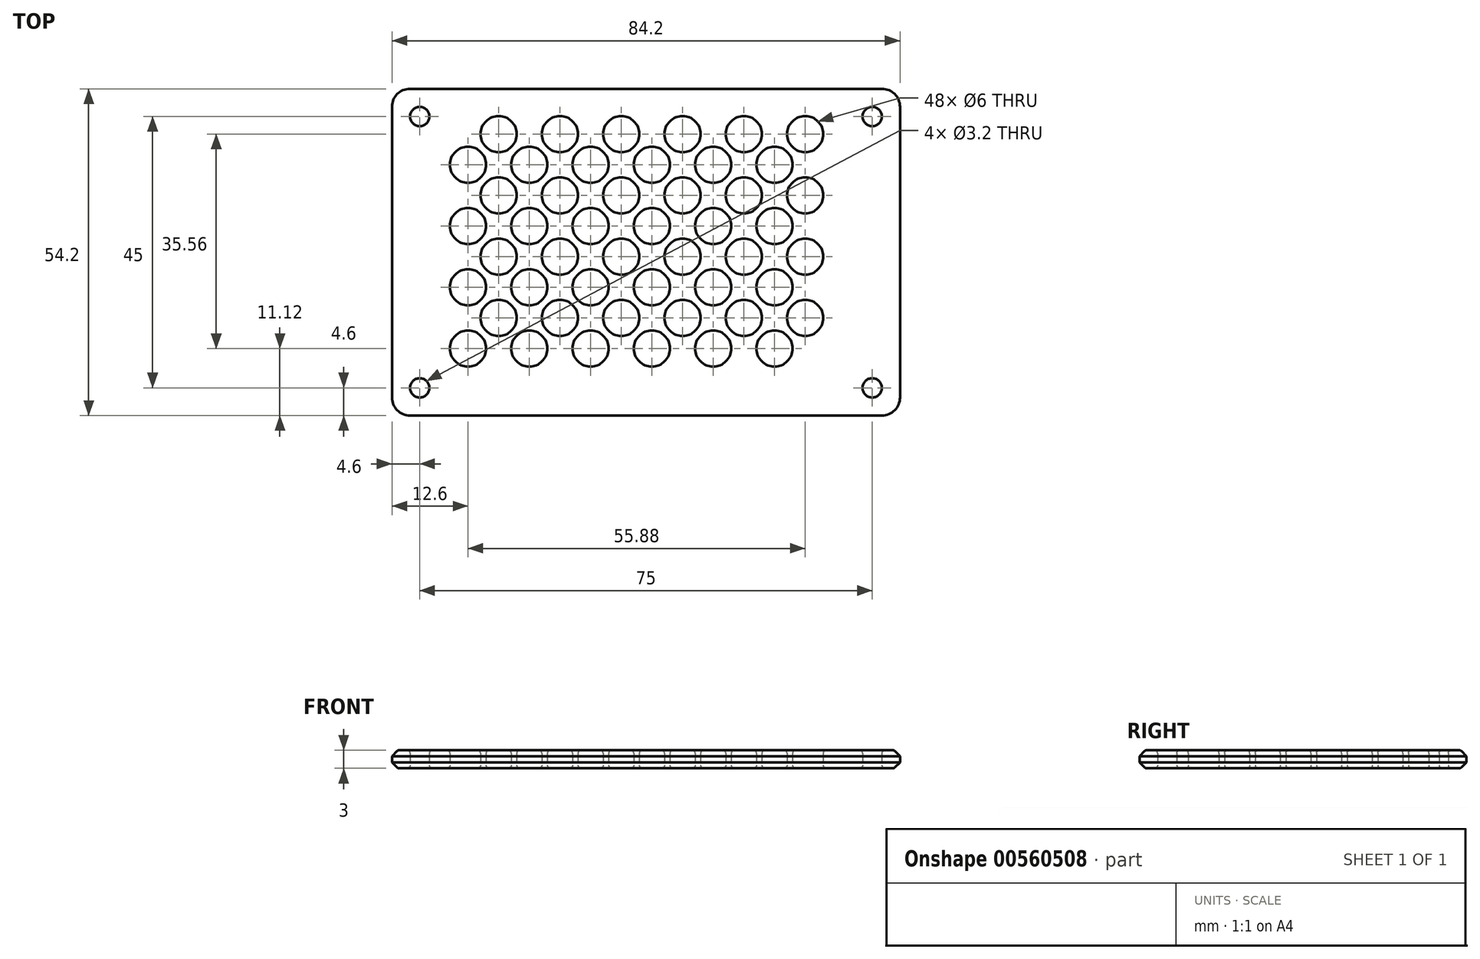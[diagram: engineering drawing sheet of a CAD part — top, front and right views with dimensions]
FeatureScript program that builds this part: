
annotation { "Feature Type Name" : "Feature", "Feature Type Description" : "" }
export const myFeature = defineFeature(function(context is Context, id is Id, definition is map)
    precondition{}
    {
        {
            var Q0;
            Q0=qCreatedBy(makeId("Top.planeOp"),FACE);
            var sketch = newSketch(context, id + "F0", { "sketchPlane" : qUnion([Q0])});
            skLineSegment(sketch, "E0.bottom", {"start": v(-42.1, 27.1) * mm, "end": v(42.1, 27.1) * mm});
            skLineSegment(sketch, "E0.top", {"start": v(-42.1, -27.1) * mm, "end": v(42.1, -27.1) * mm});
            skLineSegment(sketch, "E0.left", {"start": v(-42.1, 27.1) * mm, "end": v(-42.1, -27.1) * mm});
            skLineSegment(sketch, "E0.right", {"start": v(42.1, 27.1) * mm, "end": v(42.1, -27.1) * mm});
            skPoint(sketch, "E0.middle", {"position": v(0, 0) * mm});
            skCircle(sketch, "E1", {"center": v(-37.5, 22.5) * mm, "radius": 1.6 * mm});
            skCircle(sketch, "E2", {"center": v(-29.5, 14.5) * mm, "radius": 3 * mm});
            skCircle(sketch, "E3", {"center": v(-24.42, 19.58) * mm, "radius": 3 * mm});
            skCircle(sketch, "E4.0.1.0", {"center": v(-24.42, 9.42) * mm, "radius": 3 * mm});
            skCircle(sketch, "E4.0.1.1", {"center": v(-29.5, 4.34) * mm, "radius": 3 * mm});
            skCircle(sketch, "E4.0.2.0", {"center": v(-24.42, -0.74) * mm, "radius": 3 * mm});
            skCircle(sketch, "E4.0.2.1", {"center": v(-29.5, -5.82) * mm, "radius": 3 * mm});
            skCircle(sketch, "E4.0.3.0", {"center": v(-24.42, -10.9) * mm, "radius": 3 * mm});
            skCircle(sketch, "E4.0.3.1", {"center": v(-29.5, -15.98) * mm, "radius": 3 * mm});
            skCircle(sketch, "E4.1.0.0", {"center": v(-14.26, 19.58) * mm, "radius": 3 * mm});
            skCircle(sketch, "E4.1.0.1", {"center": v(-19.34, 14.5) * mm, "radius": 3 * mm});
            skCircle(sketch, "E4.1.1.0", {"center": v(-14.26, 9.42) * mm, "radius": 3 * mm});
            skCircle(sketch, "E4.1.1.1", {"center": v(-19.34, 4.34) * mm, "radius": 3 * mm});
            skCircle(sketch, "E4.1.2.0", {"center": v(-14.26, -0.74) * mm, "radius": 3 * mm});
            skCircle(sketch, "E4.1.2.1", {"center": v(-19.34, -5.82) * mm, "radius": 3 * mm});
            skCircle(sketch, "E4.1.3.0", {"center": v(-14.26, -10.9) * mm, "radius": 3 * mm});
            skCircle(sketch, "E4.1.3.1", {"center": v(-19.34, -15.98) * mm, "radius": 3 * mm});
            skCircle(sketch, "E4.2.0.0", {"center": v(-4.1, 19.58) * mm, "radius": 3 * mm});
            skCircle(sketch, "E4.2.0.1", {"center": v(-9.18, 14.5) * mm, "radius": 3 * mm});
            skCircle(sketch, "E4.2.1.0", {"center": v(-4.1, 9.42) * mm, "radius": 3 * mm});
            skCircle(sketch, "E4.2.1.1", {"center": v(-9.18, 4.34) * mm, "radius": 3 * mm});
            skCircle(sketch, "E4.2.2.0", {"center": v(-4.1, -0.74) * mm, "radius": 3 * mm});
            skCircle(sketch, "E4.2.2.1", {"center": v(-9.18, -5.82) * mm, "radius": 3 * mm});
            skCircle(sketch, "E4.2.3.0", {"center": v(-4.1, -10.9) * mm, "radius": 3 * mm});
            skCircle(sketch, "E4.2.3.1", {"center": v(-9.18, -15.98) * mm, "radius": 3 * mm});
            skCircle(sketch, "E4.3.0.0", {"center": v(6.06, 19.58) * mm, "radius": 3 * mm});
            skCircle(sketch, "E4.3.0.1", {"center": v(0.98, 14.5) * mm, "radius": 3 * mm});
            skCircle(sketch, "E4.3.1.0", {"center": v(6.06, 9.42) * mm, "radius": 3 * mm});
            skCircle(sketch, "E4.3.1.1", {"center": v(0.98, 4.34) * mm, "radius": 3 * mm});
            skCircle(sketch, "E4.3.2.0", {"center": v(6.06, -0.74) * mm, "radius": 3 * mm});
            skCircle(sketch, "E4.3.2.1", {"center": v(0.98, -5.82) * mm, "radius": 3 * mm});
            skCircle(sketch, "E4.3.3.0", {"center": v(6.06, -10.9) * mm, "radius": 3 * mm});
            skCircle(sketch, "E4.3.3.1", {"center": v(0.98, -15.98) * mm, "radius": 3 * mm});
            skCircle(sketch, "E4.4.0.0", {"center": v(16.22, 19.58) * mm, "radius": 3 * mm});
            skCircle(sketch, "E4.4.0.1", {"center": v(11.14, 14.5) * mm, "radius": 3 * mm});
            skCircle(sketch, "E4.4.1.0", {"center": v(16.22, 9.42) * mm, "radius": 3 * mm});
            skCircle(sketch, "E4.4.1.1", {"center": v(11.14, 4.34) * mm, "radius": 3 * mm});
            skCircle(sketch, "E4.4.2.0", {"center": v(16.22, -0.74) * mm, "radius": 3 * mm});
            skCircle(sketch, "E4.4.2.1", {"center": v(11.14, -5.82) * mm, "radius": 3 * mm});
            skCircle(sketch, "E4.4.3.0", {"center": v(16.22, -10.9) * mm, "radius": 3 * mm});
            skCircle(sketch, "E4.4.3.1", {"center": v(11.14, -15.98) * mm, "radius": 3 * mm});
            skCircle(sketch, "E4.5.0.0", {"center": v(26.38, 19.58) * mm, "radius": 3 * mm});
            skCircle(sketch, "E4.5.0.1", {"center": v(21.3, 14.5) * mm, "radius": 3 * mm});
            skCircle(sketch, "E4.5.1.0", {"center": v(26.38, 9.42) * mm, "radius": 3 * mm});
            skCircle(sketch, "E4.5.1.1", {"center": v(21.3, 4.34) * mm, "radius": 3 * mm});
            skCircle(sketch, "E4.5.2.0", {"center": v(26.38, -0.74) * mm, "radius": 3 * mm});
            skCircle(sketch, "E4.5.2.1", {"center": v(21.3, -5.82) * mm, "radius": 3 * mm});
            skCircle(sketch, "E4.5.3.0", {"center": v(26.38, -10.9) * mm, "radius": 3 * mm});
            skCircle(sketch, "E4.5.3.1", {"center": v(21.3, -15.98) * mm, "radius": 3 * mm});
            skLineSegment(sketch, "E4.direction1", {"start": v(-29.5, 14.5) * mm, "end": v(-19.34, 14.5) * mm, "construction": true});
            skLineSegment(sketch, "E4.direction2", {"start": v(-29.5, 14.5) * mm, "end": v(-29.5, 4.34) * mm, "construction": true});
            skCircle(sketch, "E5", {"center": v(37.5, 22.5) * mm, "radius": 1.6 * mm});
            skCircle(sketch, "E6", {"center": v(37.5, -22.5) * mm, "radius": 1.6 * mm});
            skCircle(sketch, "E7", {"center": v(-37.5, -22.5) * mm, "radius": 1.6 * mm});
            skSolve(sketch);
        }
        {
            var Q0;
            Q0=makeQuery(id+"F0.imprint","IMPRINT",FACE,{"disambiguationData":[TD([[makeQuery(id+"F0.imprint","IMPRINT",EDGE,{"derivedFrom":sQuery(id+"F0.wireOp",EDGE,"E0.bottom")}),-1.0]])]});
            extrude(context, id + "F1", {"entities" : qUnion([Q0]), "depth" : 3 * mm, "offsetDistance" : 25 * mm});
        }
        {
            var Q0;
            Q0=makeQuery(id+"F1.opExtrude","SWEPT_EDGE",EDGE,{"disambiguationData":[OSD([sQuery(id+"F0.wireOp",EDGE,"E0.bottom"),sQuery(id+"F0.wireOp",EDGE,"E0.left")])]});
            var Q1;
            Q1=makeQuery(id+"F1.opExtrude","SWEPT_EDGE",EDGE,{"disambiguationData":[OSD([sQuery(id+"F0.wireOp",EDGE,"E0.top"),sQuery(id+"F0.wireOp",EDGE,"E0.left")])]});
            var Q2;
            Q2=makeQuery(id+"F1.opExtrude","SWEPT_EDGE",EDGE,{"disambiguationData":[OSD([sQuery(id+"F0.wireOp",EDGE,"E0.top"),sQuery(id+"F0.wireOp",EDGE,"E0.right")])]});
            var Q3;
            Q3=makeQuery(id+"F1.opExtrude","SWEPT_EDGE",EDGE,{"disambiguationData":[OSD([sQuery(id+"F0.wireOp",EDGE,"E0.bottom"),sQuery(id+"F0.wireOp",EDGE,"E0.right")])]});
            fillet(context, id + "F2", {"entities" : qUnion([Q0, Q1, Q2, Q3]), "radius" : 3 * mm, "tangentPropagation" : true, "allowEdgeOverflow" : false});
        }
        {
            var Q0;
            Q0=makeQuery(id+"F1.opExtrude","CAP_EDGE",EDGE,{"disambiguationData":[OSD([sQuery(id+"F0.wireOp",EDGE,"E0.bottom")])],"isStart":false});
            var Q1;
            Q1=makeQuery(id+"F1.opExtrude","CAP_EDGE",EDGE,{"disambiguationData":[OSD([sQuery(id+"F0.wireOp",EDGE,"E0.bottom")])],"isStart":true});
            chamfer(context, id + "F3", {"entities" : qUnion([Q0, Q1]), "width" : 1 * mm, "tangentPropagation" : true});
        }
        {
            var Q0;
            Q0=makeQuery(id+"F1.opExtrude","CAP_FACE",FACE,{"disambiguationData":[OSD([sQuery(id+"F0.wireOp",EDGE,"E0.bottom"),sQuery(id+"F0.wireOp",EDGE,"E0.top"),sQuery(id+"F0.wireOp",EDGE,"E0.left"),sQuery(id+"F0.wireOp",EDGE,"E0.right"),sQuery(id+"F0.wireOp",EDGE,"E1"),sQuery(id+"F0.wireOp",EDGE,"E2"),sQuery(id+"F0.wireOp",EDGE,"E3"),sQuery(id+"F0.wireOp",EDGE,"E4.0.1.0"),sQuery(id+"F0.wireOp",EDGE,"E4.0.1.1"),sQuery(id+"F0.wireOp",EDGE,"E4.0.2.0"),sQuery(id+"F0.wireOp",EDGE,"E4.0.2.1"),sQuery(id+"F0.wireOp",EDGE,"E4.0.3.0"),sQuery(id+"F0.wireOp",EDGE,"E4.0.3.1"),sQuery(id+"F0.wireOp",EDGE,"E4.1.0.0"),sQuery(id+"F0.wireOp",EDGE,"E4.1.0.1"),sQuery(id+"F0.wireOp",EDGE,"E4.1.1.0"),sQuery(id+"F0.wireOp",EDGE,"E4.1.1.1"),sQuery(id+"F0.wireOp",EDGE,"E4.1.2.0"),sQuery(id+"F0.wireOp",EDGE,"E4.1.2.1"),sQuery(id+"F0.wireOp",EDGE,"E4.1.3.0"),sQuery(id+"F0.wireOp",EDGE,"E4.1.3.1"),sQuery(id+"F0.wireOp",EDGE,"E4.2.0.0"),sQuery(id+"F0.wireOp",EDGE,"E4.2.0.1"),sQuery(id+"F0.wireOp",EDGE,"E4.2.1.0"),sQuery(id+"F0.wireOp",EDGE,"E4.2.1.1"),sQuery(id+"F0.wireOp",EDGE,"E4.2.2.0"),sQuery(id+"F0.wireOp",EDGE,"E4.2.2.1"),sQuery(id+"F0.wireOp",EDGE,"E4.2.3.0"),sQuery(id+"F0.wireOp",EDGE,"E4.2.3.1"),sQuery(id+"F0.wireOp",EDGE,"E4.3.0.0"),sQuery(id+"F0.wireOp",EDGE,"E4.3.0.1"),sQuery(id+"F0.wireOp",EDGE,"E4.3.1.0"),sQuery(id+"F0.wireOp",EDGE,"E4.3.1.1"),sQuery(id+"F0.wireOp",EDGE,"E4.3.2.0"),sQuery(id+"F0.wireOp",EDGE,"E4.3.2.1"),sQuery(id+"F0.wireOp",EDGE,"E4.3.3.0"),sQuery(id+"F0.wireOp",EDGE,"E4.3.3.1"),sQuery(id+"F0.wireOp",EDGE,"E4.4.0.0"),sQuery(id+"F0.wireOp",EDGE,"E4.4.0.1"),sQuery(id+"F0.wireOp",EDGE,"E4.4.1.0"),sQuery(id+"F0.wireOp",EDGE,"E4.4.1.1"),sQuery(id+"F0.wireOp",EDGE,"E4.4.2.0"),sQuery(id+"F0.wireOp",EDGE,"E4.4.2.1"),sQuery(id+"F0.wireOp",EDGE,"E4.4.3.0"),sQuery(id+"F0.wireOp",EDGE,"E4.4.3.1"),sQuery(id+"F0.wireOp",EDGE,"E4.5.0.0"),sQuery(id+"F0.wireOp",EDGE,"E4.5.0.1"),sQuery(id+"F0.wireOp",EDGE,"E4.5.1.0"),sQuery(id+"F0.wireOp",EDGE,"E4.5.1.1"),sQuery(id+"F0.wireOp",EDGE,"E4.5.2.0"),sQuery(id+"F0.wireOp",EDGE,"E4.5.2.1"),sQuery(id+"F0.wireOp",EDGE,"E4.5.3.0"),sQuery(id+"F0.wireOp",EDGE,"E4.5.3.1"),sQuery(id+"F0.wireOp",EDGE,"E5"),sQuery(id+"F0.wireOp",EDGE,"E6"),sQuery(id+"F0.wireOp",EDGE,"E7")])],"isStart":false});
            var Q1;
            Q1=makeQuery(id+"F1.opExtrude","CAP_FACE",FACE,{"disambiguationData":[OSD([sQuery(id+"F0.wireOp",EDGE,"E0.bottom"),sQuery(id+"F0.wireOp",EDGE,"E0.top"),sQuery(id+"F0.wireOp",EDGE,"E0.left"),sQuery(id+"F0.wireOp",EDGE,"E0.right"),sQuery(id+"F0.wireOp",EDGE,"E1"),sQuery(id+"F0.wireOp",EDGE,"E2"),sQuery(id+"F0.wireOp",EDGE,"E3"),sQuery(id+"F0.wireOp",EDGE,"E4.0.1.0"),sQuery(id+"F0.wireOp",EDGE,"E4.0.1.1"),sQuery(id+"F0.wireOp",EDGE,"E4.0.2.0"),sQuery(id+"F0.wireOp",EDGE,"E4.0.2.1"),sQuery(id+"F0.wireOp",EDGE,"E4.0.3.0"),sQuery(id+"F0.wireOp",EDGE,"E4.0.3.1"),sQuery(id+"F0.wireOp",EDGE,"E4.1.0.0"),sQuery(id+"F0.wireOp",EDGE,"E4.1.0.1"),sQuery(id+"F0.wireOp",EDGE,"E4.1.1.0"),sQuery(id+"F0.wireOp",EDGE,"E4.1.1.1"),sQuery(id+"F0.wireOp",EDGE,"E4.1.2.0"),sQuery(id+"F0.wireOp",EDGE,"E4.1.2.1"),sQuery(id+"F0.wireOp",EDGE,"E4.1.3.0"),sQuery(id+"F0.wireOp",EDGE,"E4.1.3.1"),sQuery(id+"F0.wireOp",EDGE,"E4.2.0.0"),sQuery(id+"F0.wireOp",EDGE,"E4.2.0.1"),sQuery(id+"F0.wireOp",EDGE,"E4.2.1.0"),sQuery(id+"F0.wireOp",EDGE,"E4.2.1.1"),sQuery(id+"F0.wireOp",EDGE,"E4.2.2.0"),sQuery(id+"F0.wireOp",EDGE,"E4.2.2.1"),sQuery(id+"F0.wireOp",EDGE,"E4.2.3.0"),sQuery(id+"F0.wireOp",EDGE,"E4.2.3.1"),sQuery(id+"F0.wireOp",EDGE,"E4.3.0.0"),sQuery(id+"F0.wireOp",EDGE,"E4.3.0.1"),sQuery(id+"F0.wireOp",EDGE,"E4.3.1.0"),sQuery(id+"F0.wireOp",EDGE,"E4.3.1.1"),sQuery(id+"F0.wireOp",EDGE,"E4.3.2.0"),sQuery(id+"F0.wireOp",EDGE,"E4.3.2.1"),sQuery(id+"F0.wireOp",EDGE,"E4.3.3.0"),sQuery(id+"F0.wireOp",EDGE,"E4.3.3.1"),sQuery(id+"F0.wireOp",EDGE,"E4.4.0.0"),sQuery(id+"F0.wireOp",EDGE,"E4.4.0.1"),sQuery(id+"F0.wireOp",EDGE,"E4.4.1.0"),sQuery(id+"F0.wireOp",EDGE,"E4.4.1.1"),sQuery(id+"F0.wireOp",EDGE,"E4.4.2.0"),sQuery(id+"F0.wireOp",EDGE,"E4.4.2.1"),sQuery(id+"F0.wireOp",EDGE,"E4.4.3.0"),sQuery(id+"F0.wireOp",EDGE,"E4.4.3.1"),sQuery(id+"F0.wireOp",EDGE,"E4.5.0.0"),sQuery(id+"F0.wireOp",EDGE,"E4.5.0.1"),sQuery(id+"F0.wireOp",EDGE,"E4.5.1.0"),sQuery(id+"F0.wireOp",EDGE,"E4.5.1.1"),sQuery(id+"F0.wireOp",EDGE,"E4.5.2.0"),sQuery(id+"F0.wireOp",EDGE,"E4.5.2.1"),sQuery(id+"F0.wireOp",EDGE,"E4.5.3.0"),sQuery(id+"F0.wireOp",EDGE,"E4.5.3.1"),sQuery(id+"F0.wireOp",EDGE,"E5"),sQuery(id+"F0.wireOp",EDGE,"E6"),sQuery(id+"F0.wireOp",EDGE,"E7")])],"isStart":true});
            fillet(context, id + "F4", {"entities" : qUnion([Q0, Q1]), "radius" : 0.5 * mm, "tangentPropagation" : true, "allowEdgeOverflow" : false});
        }
    });
